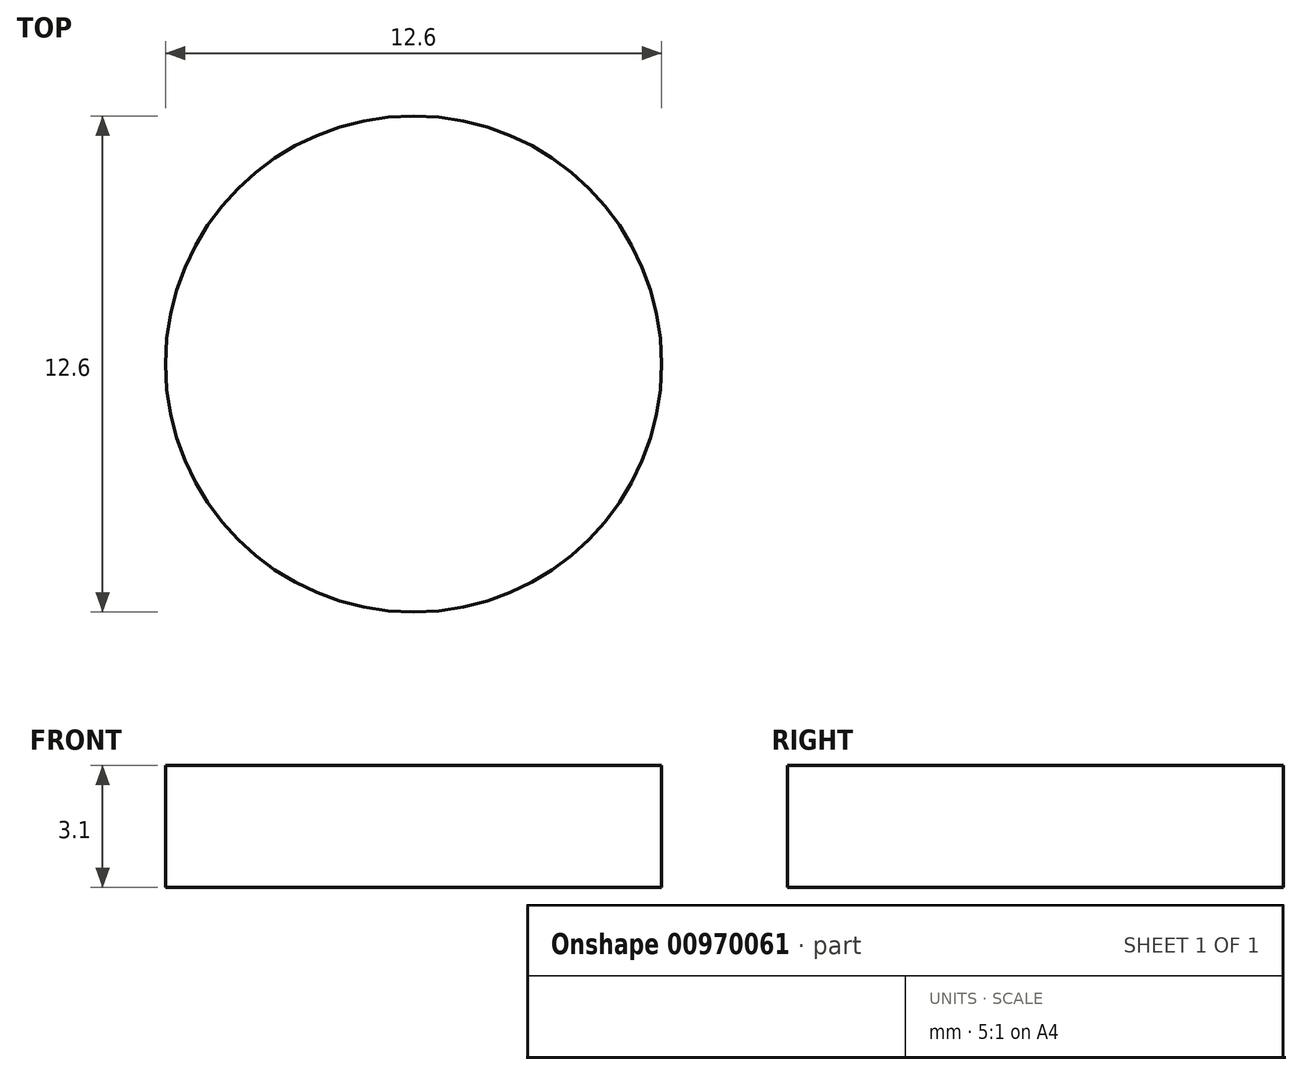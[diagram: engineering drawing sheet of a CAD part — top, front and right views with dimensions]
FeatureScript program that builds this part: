
annotation { "Feature Type Name" : "Feature", "Feature Type Description" : "" }
export const myFeature = defineFeature(function(context is Context, id is Id, definition is map)
    precondition{}
    {
        {
            var Q0;
            Q0=qCreatedBy(makeId("Top.planeOp"),FACE);
            var sketch = newSketch(context, id + "F0", { "sketchPlane" : qUnion([Q0])});
            skCircle(sketch, "E0", {"center": v(0, 0) * mm, "radius": 6.3 * mm});
            skSolve(sketch);
        }
        {
            var Q0;
            Q0=makeQuery(id+"F0.imprint","IMPRINT",FACE,{"disambiguationData":[TD([[makeQuery(id+"F0.imprint","IMPRINT",EDGE,{"derivedFrom":sQuery(id+"F0.wireOp",EDGE,"E0")}),1.0]])]});
            extrude(context, id + "F1", {"entities" : qUnion([Q0]), "depth" : 3.1 * mm, "offsetDistance" : 25 * mm});
        }
    });
